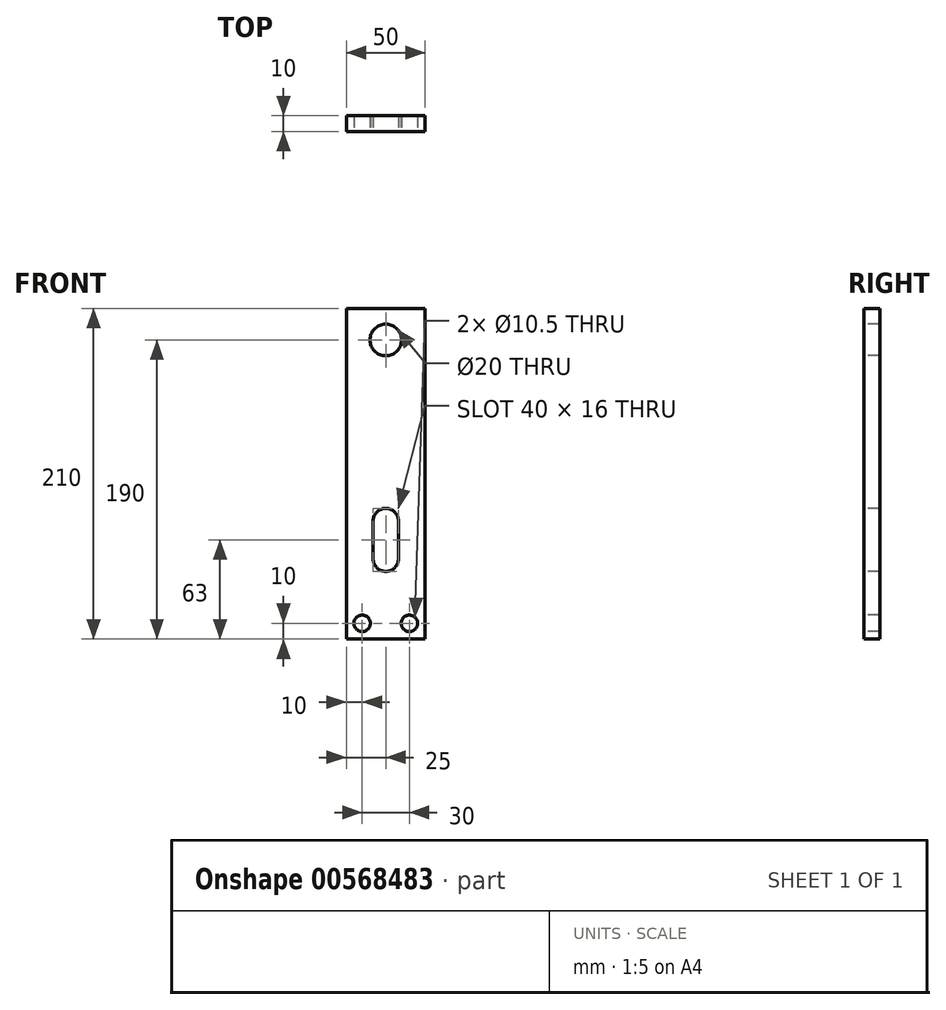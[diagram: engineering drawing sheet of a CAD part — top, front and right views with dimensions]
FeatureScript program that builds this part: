
annotation { "Feature Type Name" : "Feature", "Feature Type Description" : "" }
export const myFeature = defineFeature(function(context is Context, id is Id, definition is map)
    precondition{}
    {
        {
            var Q0;
            Q0=qCreatedBy(makeId("Front.planeOp"),FACE);
            var sketch = newSketch(context, id + "F0", { "sketchPlane" : qUnion([Q0])});
            skLineSegment(sketch, "E0.bottom", {"start": v(-25, 105) * mm, "end": v(25, 105) * mm});
            skLineSegment(sketch, "E0.top", {"start": v(-25, -105) * mm, "end": v(25, -105) * mm});
            skLineSegment(sketch, "E0.left", {"start": v(-25, 105) * mm, "end": v(-25, -105) * mm});
            skLineSegment(sketch, "E0.right", {"start": v(25, 105) * mm, "end": v(25, -105) * mm});
            skLineSegment(sketch, "E1", {"start": v(0, 75.07) * mm, "end": v(0, 0) * mm, "construction": true});
            skLineSegment(sketch, "E2", {"start": v(0, 0) * mm, "end": v(68.64, 0) * mm, "construction": true});
            skSolve(sketch);
        }
        {
            var Q0;
            Q0=makeQuery(id+"F0.imprint","IMPRINT",FACE,{"disambiguationData":[TD([[makeQuery(id+"F0.imprint","IMPRINT",EDGE,{"derivedFrom":sQuery(id+"F0.wireOp",EDGE,"E0.bottom")}),-1.0]])]});
            extrude(context, id + "F1", {"entities" : qUnion([Q0]), "endBound" : BoundingType.SYMMETRIC, "depth" : 10 * mm, "offsetDistance" : 25 * mm});
        }
        {
            var Q0;
            Q0=makeQuery(id+"F1.opExtrude","CAP_FACE",FACE,{"disambiguationData":[OSD([sQuery(id+"F0.wireOp",EDGE,"E0.bottom"),sQuery(id+"F0.wireOp",EDGE,"E0.top"),sQuery(id+"F0.wireOp",EDGE,"E0.left"),sQuery(id+"F0.wireOp",EDGE,"E0.right")])],"isStart":false});
            var sketch = newSketch(context, id + "F2", { "sketchPlane" : qUnion([Q0])});
            skPoint(sketch, "E3", {"position": v(0, 85) * mm});
            skPoint(sketch, "E4", {"position": v(-9.93, -56.94) * mm});
            skPoint(sketch, "E5", {"position": v(9.42, -56.94) * mm});
            skArc(sketch, "E6", {"start": v(8, -30) * mm, "mid": v(0, -22) * mm, "end": v(-8, -30) * mm});
            skArc(sketch, "E7", {"start": v(-8, -54) * mm, "mid": v(0, -62) * mm, "end": v(8, -54) * mm});
            skLineSegment(sketch, "E8.left", {"start": v(-8, -30) * mm, "end": v(-8, -54) * mm});
            skLineSegment(sketch, "E8.right", {"start": v(8, -30) * mm, "end": v(8, -54) * mm});
            skPoint(sketch, "E9", {"position": v(0, -45) * mm});
            skSolve(sketch);
        }
        {
            var Q0;
            Q0=sQuery(id+"F2.wireOp",VERTEX,"E3");
            var Q1;
            Q1=makeQuery(id+"F1.opExtrude","SWEPT_BODY",BODY,{"disambiguationData":[OSD([sQuery(id+"F0.wireOp",EDGE,"E0.bottom"),sQuery(id+"F0.wireOp",EDGE,"E0.top"),sQuery(id+"F0.wireOp",EDGE,"E0.left"),sQuery(id+"F0.wireOp",EDGE,"E0.right")])]});
            hole(context, id + "F3", {"style" : HoleStyle.SIMPLE, "endStyle" : HoleEndStyle.THROUGH, "holeDiameter" : 20 * mm, "isTappedThrough" : true, "tappedDepth" : 12 * mm, "tapClearance" : 3, "locations" : qUnion([Q0]), "scope" : qUnion([Q1])});
        }
        {
            var Q0;
            Q0=makeQuery(id+"F2.imprint","IMPRINT",FACE,{"disambiguationData":[TD([[makeQuery(id+"F2.imprint","IMPRINT",EDGE,{"derivedFrom":sQuery(id+"F2.wireOp",EDGE,"E6")}),1.0]])]});
            var Q1;
            Q1=makeQuery(id+"F1.opExtrude","CAP_FACE",FACE,{"disambiguationData":[OSD([sQuery(id+"F0.wireOp",EDGE,"E0.bottom"),sQuery(id+"F0.wireOp",EDGE,"E0.top"),sQuery(id+"F0.wireOp",EDGE,"E0.left"),sQuery(id+"F0.wireOp",EDGE,"E0.right")])],"isStart":true});
            extrude(context, id + "F4", {"entities" : qUnion([Q0]), "operationType" : NewBodyOperationType.REMOVE, "endBound" : BoundingType.UP_TO_SURFACE, "oppositeDirection" : true, "depth" : 25 * mm, "endBoundEntityFace" : qUnion([Q1]), "offsetDistance" : 25 * mm});
        }
        {
            var Q0;
            Q0=makeQuery(id+"F2.imprint","IMPRINT",FACE,{"disambiguationData":[TD([[makeQuery(id+"F2.imprint","IMPRINT",EDGE,{"derivedFrom":sQuery(id+"F2.wireOp",EDGE,"E6")}),-1.0]])]});
            var sketch = newSketch(context, id + "F5", { "sketchPlane" : qUnion([Q0])});
            skPoint(sketch, "E10", {"position": v(-15, -95) * mm});
            skPoint(sketch, "E11", {"position": v(15, -95) * mm});
            skSolve(sketch);
        }
        {
            var Q0;
            Q0=sQuery(id+"F5.wireOp",VERTEX,"E10");
            var Q1;
            Q1=sQuery(id+"F5.wireOp",VERTEX,"E11");
            var Q2;
            Q2=makeQuery(id+"F1.opExtrude","SWEPT_BODY",BODY,{"disambiguationData":[OSD([sQuery(id+"F0.wireOp",EDGE,"E0.bottom"),sQuery(id+"F0.wireOp",EDGE,"E0.top"),sQuery(id+"F0.wireOp",EDGE,"E0.left"),sQuery(id+"F0.wireOp",EDGE,"E0.right")])]});
            hole(context, id + "F6", {"style" : HoleStyle.SIMPLE, "endStyle" : HoleEndStyle.THROUGH, "holeDiameter" : 10.5 * mm, "isTappedThrough" : true, "tappedDepth" : 12 * mm, "tapClearance" : 3, "locations" : qUnion([Q0, Q1]), "scope" : qUnion([Q2]), "majorDiameter" : 5 * mm});
        }
    });
